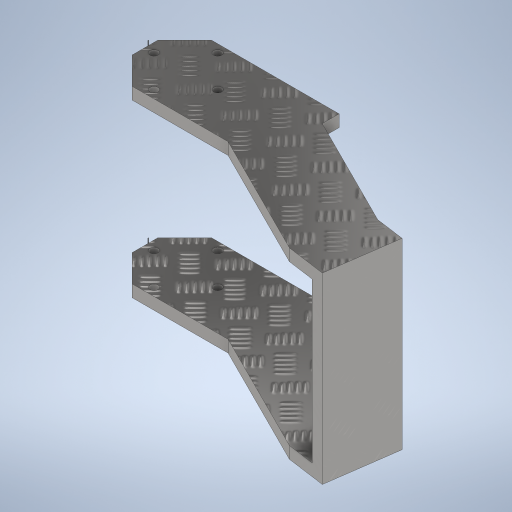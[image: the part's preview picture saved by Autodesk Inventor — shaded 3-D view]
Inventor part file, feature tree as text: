
AUTODESK INVENTOR PART (.ipt)
format: ipt  version: 2024 (Build 280153000, 153)  size: 373,248 bytes
history: native  units: in
note: dims shown in document units (in); Inventor stores cm internally (conversion verified against a paired STEP export)
features: extrude x5, sketch x5
ambient origin geometry x8: Origin, YZ Plane, XZ Plane, XY Plane, X Axis, Y Axis, Z Axis, Center Point
bodies: Solid1 (feature_tree)
feature tree (10):
  extrude  "Extrusion1"  Depth=0.7874in
  extrude  "Extrusion2"  Depth=0.2362in
  extrude  "Extrusion3"  Depth=0.2362in
  extrude  "Extrusion4"  Depth=0.1181in
  extrude  "Extrusion6"  Depth=0.0472in
  sketch  "Sketch1"  dims[d0=1.5748in d1=0.7874in]
  sketch  "Sketch2"  dims[d2=0.2362in d3=0.2362in]
  sketch  "Sketch3"  dims[d4=0.2362in d5=0.2362in]
  sketch  "Sketch4"  dims[d6=0.1181in d7=0.0in d8=0.1181in]
  sketch  "Sketch7"  dims[d9=1.5748in d10=0.0in d11=1.1089in d12=1.5748in d13=0.2362in d14=0.2362in d15=0.2362in d16=0.2362in d17=0.1181in d18=0.0in d19=0.4528in d20=0.0787in d21=0.315in d22=1.5748in d24=360.0deg d26=1.9685in d27=0.0in d28=0.315in d29=0.315in d30=0.315in d31=0.315in d32=0.315in d33=0.315in d34=0.315in d35=0.315in d40=0.0472in d41=1.9685in d42=0.0in]
